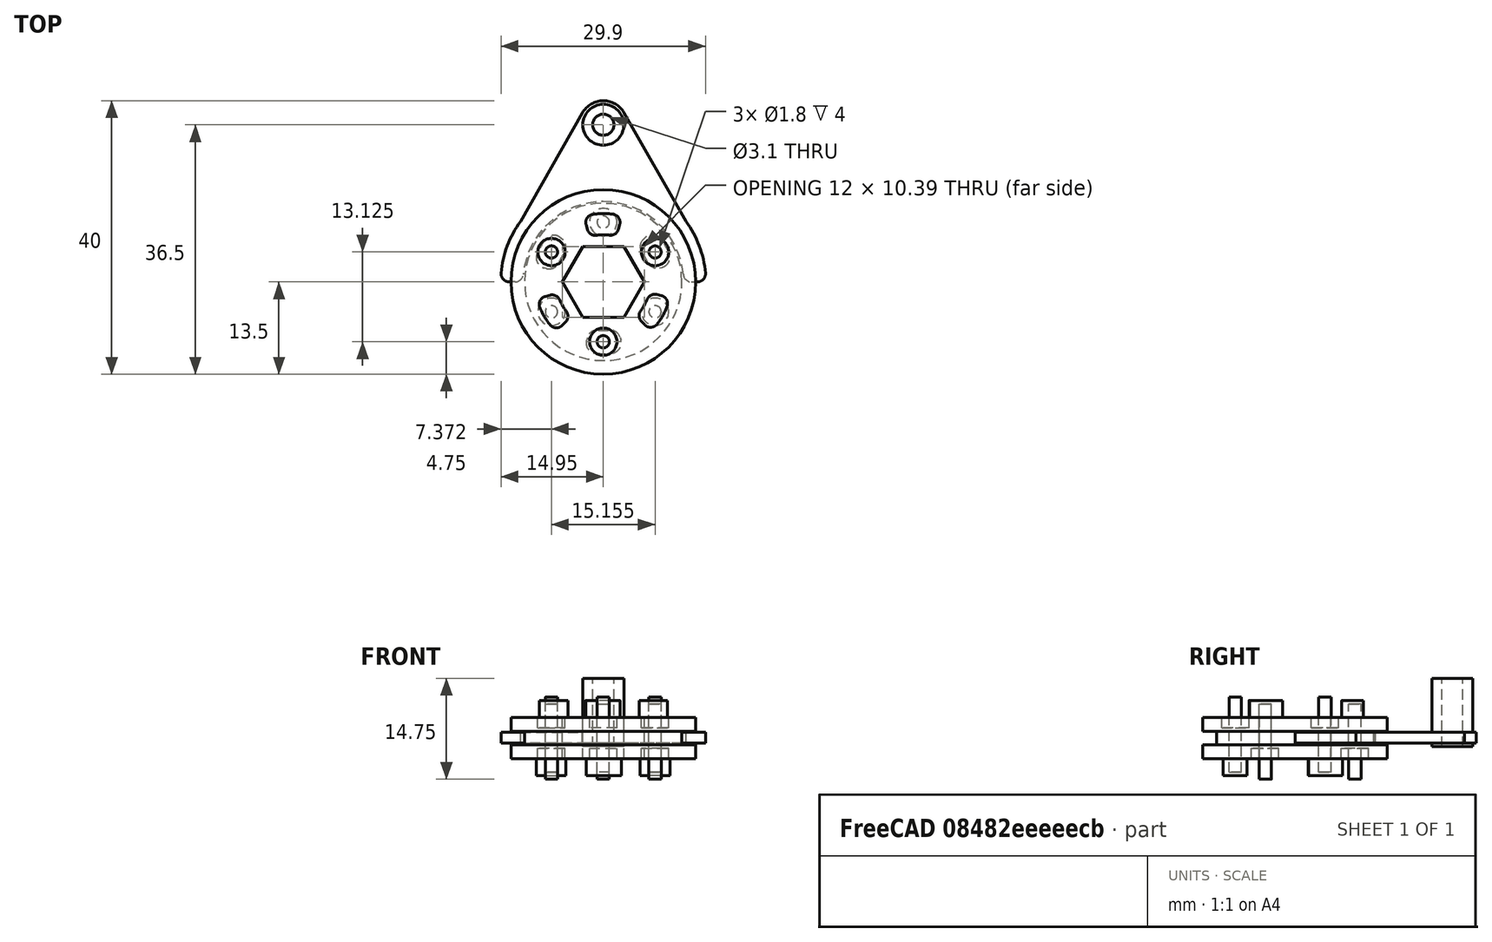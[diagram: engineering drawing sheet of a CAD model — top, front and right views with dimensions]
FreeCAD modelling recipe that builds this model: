
FCSTD DOCUMENT  (FreeCAD 0.16R5694 (Git))
Label: gearbox-selector
License: All rights reserved
LicenseURL: http://en.wikipedia.org/wiki/All_rights_reserved
objects: Part::Cylinder×44, Part::MultiFuse×15, Part::Cut×12, Part::Fillet×7, Part::Box×5, Part::Feature×3, Part::Extrusion×3, Part::RegularPolygon×1, Part::Mirroring×1
note: 91 computed .brp shape members not serialized (recipe doc carries the construction recipe); baked Part::Feature solids carry a one-line shape summary decoded from their .brp

FEATURE [Part::Cylinder] Cylinder
  Angle = 360
  Height = 2
  Radius = 13.5
FEATURE [Part::RegularPolygon] RegularPolygon  label="Regular polygon"
  Circumradius = 6
  Polygon = 6
FEATURE [Part::Feature] Face
  shape: bbox 18.03 x 18.03 x 2e-07 mm, 1 faces, 0 solids (baked)
FEATURE [Part::Extrusion] Extrude
  Base = -> Face
  Dir = (0,0,6)
  Solid = false
FEATURE [Part::Cylinder] Cylinder001
  Angle = 360
  Height = 2
  Placement = pos=(0,0,2) rot=(0,0,1;0rad)
  Radius = 11.5
FEATURE [Part::Cylinder] Cylinder002
  Angle = 360
  Height = 2
  Placement = pos=(0,0,4) rot=(0,0,1;0rad)
  Radius = 13.5
FEATURE [Part::Feature] Face001
  shape: bbox 18.03 x 18.03 x 2e-07 mm, 1 faces, 0 solids (baked)
FEATURE [Part::Extrusion] Extrude001
  Base = -> Face001
  Dir = (0,0,6)
  Solid = false
FEATURE [Part::Cut] Cut
  Base = -> Cylinder001
  Tool = -> Extrude
FEATURE [Part::Feature] Face002
  shape: bbox 18.03 x 18.03 x 2e-07 mm, 1 faces, 0 solids (baked)
FEATURE [Part::Extrusion] Extrude002
  Base = -> Face002
  Dir = (0,0,6)
  Solid = false
FEATURE [Part::Cut] Cut001
  Base = -> Cylinder
  Tool = -> Extrude001
FEATURE [Part::Cut] Cut002
  Base = -> Cylinder002
  Tool = -> Extrude002
FEATURE [Part::Cylinder] Cylinder003
  Angle = 32.74
  Height = 2.5
  Radius = 10.5
FEATURE [Part::Cylinder] Cylinder004
  Angle = 32.74
  Height = 2.5
  Radius = 7.1
FEATURE [Part::Cut] Cut003
  Base = -> Cylinder003
  Placement = pos=(0,0,-2.5) rot=(0,0,1;0.244346rad)
  Tool = -> Cylinder004
FEATURE [Part::Fillet] Fillet
  Base = -> Cut003
  Edges = 4 edges r=1.5: [Edge2,Edge4,Edge9,Edge12]
FEATURE [Part::Cylinder] Cylinder005
  Angle = 32.74
  Height = 2.5
  Radius = 10
FEATURE [Part::Cylinder] Cylinder006
  Angle = 32.74
  Height = 2.5
  Radius = 6.9
FEATURE [Part::Cut] Cut004
  Base = -> Cylinder005
  Placement = pos=(0,0,-2.5) rot=(0,0,1;0.244346rad)
  Tool = -> Cylinder006
FEATURE [Part::Fillet] Fillet001
  Base = -> Cut004
  Edges = 4 edges r=1.2: [Edge2,Edge4,Edge9,Edge12]
  Placement = pos=(0,0,8.5) rot=(0,0,1;0rad)
FEATURE [Part::Cylinder] Cylinder007
  Angle = 32.74
  Height = 2.5
  Radius = 10.5
FEATURE [Part::Cylinder] Cylinder008
  Angle = 32.74
  Height = 2.5
  Radius = 7.1
FEATURE [Part::Cut] Cut005
  Base = -> Cylinder007
  Placement = pos=(0,0,-2.5) rot=(0,0,1;0.244346rad)
  Tool = -> Cylinder008
FEATURE [Part::Fillet] Fillet002
  Base = -> Cut005
  Edges = 4 edges r=1.5: [Edge2,Edge4,Edge9,Edge12]
  Placement = pos=(0,0,0) rot=(0,0,1;2.0944rad)
FEATURE [Part::Cylinder] Cylinder009
  Angle = 32.74
  Height = 2.5
  Radius = 10.5
FEATURE [Part::Cylinder] Cylinder010
  Angle = 32.74
  Height = 2.5
  Radius = 7.1
FEATURE [Part::Cut] Cut006
  Base = -> Cylinder009
  Placement = pos=(0,0,-2.5) rot=(0,0,1;0.244346rad)
  Tool = -> Cylinder010
FEATURE [Part::Fillet] Fillet003
  Base = -> Cut006
  Edges = 4 edges r=1.5: [Edge2,Edge4,Edge9,Edge12]
  Placement = pos=(0,0,0) rot=(0,0,-1;2.0944rad)
FEATURE [Part::MultiFuse] Fusion
  Shapes = -> [Fillet003,Fillet002,Fillet]
FEATURE [Part::Cylinder] Cylinder011
  Angle = 32.74
  Height = 2.5
  Radius = 10
FEATURE [Part::Cylinder] Cylinder012
  Angle = 32.74
  Height = 2.5
  Radius = 6.9
FEATURE [Part::Cut] Cut007
  Base = -> Cylinder011
  Placement = pos=(0,0,-2.5) rot=(0,0,1;0.244346rad)
  Tool = -> Cylinder012
FEATURE [Part::Fillet] Fillet004
  Base = -> Cut007
  Edges = 4 edges r=1.2: [Edge2,Edge4,Edge9,Edge12]
  Placement = pos=(0,0,8.5) rot=(0,0,1;2.0944rad)
FEATURE [Part::Cylinder] Cylinder013
  Angle = 32.74
  Height = 2.5
  Radius = 10
FEATURE [Part::Cylinder] Cylinder014
  Angle = 32.74
  Height = 2.5
  Radius = 6.9
FEATURE [Part::Cut] Cut008
  Base = -> Cylinder013
  Placement = pos=(0,0,-2.5) rot=(0,0,1;0.244346rad)
  Tool = -> Cylinder014
FEATURE [Part::Fillet] Fillet005
  Base = -> Cut008
  Edges = 4 edges r=1.2: [Edge2,Edge4,Edge9,Edge12]
  Placement = pos=(0,0,8.5) rot=(0,0,-1;2.0944rad)
FEATURE [Part::MultiFuse] Fusion001
  Placement = pos=(0,0,0) rot=(0,0,1;1.0472rad)
  Shapes = -> [Fillet001,Fillet004,Fillet005]
FEATURE [Part::Cylinder] Cylinder015
  Angle = 360
  Height = 11
  Placement = pos=(0,-8.75,-2.5) rot=(0,0,1;0rad)
  Radius = 0.9
FEATURE [Part::Cylinder] Cylinder016
  Angle = 360
  Height = 11
  Placement = pos=(7.57772,-4.375,-2.5) rot=(0,0,1;1.0472rad)
  Radius = 0.9
FEATURE [Part::Cylinder] Cylinder017
  Angle = 360
  Height = 11
  Placement = pos=(7.57772,4.375,-2.5) rot=(0,0,1;2.0944rad)
  Radius = 0.9
FEATURE [Part::Cylinder] Cylinder018
  Angle = 360
  Height = 11
  Placement = pos=(0,8.75,-2.5) rot=(0,0,1;3.14159rad)
  Radius = 0.9
FEATURE [Part::Cylinder] Cylinder019
  Angle = 360
  Height = 11
  Placement = pos=(-7.57772,4.375,-2.5) rot=(0,0,1;4.18879rad)
  Radius = 0.9
FEATURE [Part::Cylinder] Cylinder020
  Angle = 360
  Height = 11
  Placement = pos=(-7.57772,-4.375,-2.5) rot=(0,0,-1;1.0472rad)
  Radius = 0.9
FEATURE [Part::MultiFuse] Fusion002
  Placement = pos=(0,0,0.5) rot=(0,0,1;0rad)
  Shapes = -> [Cylinder015,Cylinder017,Cylinder019]
FEATURE [Part::MultiFuse] Fusion003
  Placement = pos=(0,0,-0.5) rot=(0,0,1;0rad)
  Shapes = -> [Cylinder016,Cylinder018,Cylinder020]
FEATURE [Part::MultiFuse] Fusion004
  Shapes = -> [Cut001,Fusion]
FEATURE [Part::MultiFuse] Fusion005
  Shapes = -> [Cut002,Fusion001]
FEATURE [Part::Cylinder] Cylinder021
  Angle = 360
  Height = 1.5
  Placement = pos=(0,-8.75,-2.5) rot=(0,0,1;0rad)
  Radius = 2
FEATURE [Part::Cylinder] Cylinder022
  Angle = 360
  Height = 1.5
  Placement = pos=(7.57772,4.375,-2.5) rot=(0,0,1;2.0944rad)
  Radius = 2
FEATURE [Part::Cylinder] Cylinder023
  Angle = 360
  Height = 1.5
  Placement = pos=(-7.57772,4.375,-2.5) rot=(0,0,-1;2.0944rad)
  Radius = 2
FEATURE [Part::MultiFuse] Fusion006
  Placement = pos=(0,0,7) rot=(0,0,1;0rad)
  Shapes = -> [Cylinder021,Cylinder022,Cylinder023]
FEATURE [Part::Cylinder] Cylinder024
  Angle = 360
  Height = 11
  Placement = pos=(0,-8.75,-2.5) rot=(0,0,1;0rad)
  Radius = 0.9
FEATURE [Part::Cylinder] Cylinder025
  Angle = 360
  Height = 11
  Placement = pos=(7.57772,4.375,-2.5) rot=(0,0,1;2.0944rad)
  Radius = 0.9
FEATURE [Part::Cylinder] Cylinder026
  Angle = 360
  Height = 11
  Placement = pos=(-7.57772,4.375,-2.5) rot=(0,0,1;4.18879rad)
  Radius = 0.9
FEATURE [Part::MultiFuse] Fusion007
  Placement = pos=(0,0,0.5) rot=(0,0,1;0rad)
  Shapes = -> [Cylinder024,Cylinder025,Cylinder026]
FEATURE [Part::Cylinder] Cylinder027
  Angle = 360
  Height = 11
  Placement = pos=(0,-8.75,-2.5) rot=(0,0,1;0rad)
  Radius = 0.9
FEATURE [Part::Cylinder] Cylinder028
  Angle = 360
  Height = 11
  Placement = pos=(7.57772,4.375,-2.5) rot=(0,0,1;2.0944rad)
  Radius = 0.9
FEATURE [Part::Cylinder] Cylinder029
  Angle = 360
  Height = 11
  Placement = pos=(-7.57772,4.375,-2.5) rot=(0,0,1;4.18879rad)
  Radius = 0.9
FEATURE [Part::MultiFuse] Fusion008
  Placement = pos=(0,0,0.5) rot=(0,0,1;0rad)
  Shapes = -> [Cylinder027,Cylinder028,Cylinder029]
FEATURE [Part::Cut] Cut012
  Base = -> Fusion004
  Tool = -> Fusion002
FEATURE [Part::Cylinder] Cylinder030
  Angle = 360
  Height = 1.5
  Placement = pos=(7.57772,-4.375,-2.5) rot=(0,0,1;1.0472rad)
  Radius = 2
FEATURE [Part::Cylinder] Cylinder031
  Angle = 360
  Height = 1.5
  Placement = pos=(0,8.75,-2.5) rot=(0,0,1;3.14159rad)
  Radius = 2
FEATURE [Part::Cylinder] Cylinder032
  Angle = 360
  Height = 1.5
  Placement = pos=(-7.57772,-4.375,-2.5) rot=(0,0,-1;1.0472rad)
  Radius = 2
FEATURE [Part::MultiFuse] Fusion009
  Placement = pos=(0,0,2.5) rot=(0,0,1;0rad)
  Shapes = -> [Cylinder030,Cylinder031,Cylinder032]
FEATURE [Part::Cylinder] Cylinder033
  Angle = 360
  Height = 11
  Placement = pos=(7.57772,-4.375,-2.5) rot=(0,0,1;1.0472rad)
  Radius = 0.9
FEATURE [Part::Cylinder] Cylinder034
  Angle = 360
  Height = 11
  Placement = pos=(0,8.75,-2.5) rot=(0,0,1;3.14159rad)
  Radius = 0.9
FEATURE [Part::Cylinder] Cylinder035
  Angle = 360
  Height = 11
  Placement = pos=(-7.57772,-4.375,-2.5) rot=(0,0,-1;1.0472rad)
  Radius = 0.9
FEATURE [Part::MultiFuse] Fusion010
  Placement = pos=(0,0,-0.5) rot=(0,0,1;0rad)
  Shapes = -> [Cylinder033,Cylinder034,Cylinder035]
FEATURE [Part::Cylinder] Cylinder036
  Angle = 360
  Height = 11
  Placement = pos=(7.57772,-4.375,-2.5) rot=(0,0,1;1.0472rad)
  Radius = 0.9
FEATURE [Part::Cylinder] Cylinder037
  Angle = 360
  Height = 11
  Placement = pos=(0,8.75,-2.5) rot=(0,0,1;3.14159rad)
  Radius = 0.9
FEATURE [Part::Cylinder] Cylinder038
  Angle = 360
  Height = 11
  Placement = pos=(-7.57772,-4.375,-2.5) rot=(0,0,-1;1.0472rad)
  Radius = 0.9
FEATURE [Part::MultiFuse] Fusion011
  Placement = pos=(0,0,-0.5) rot=(0,0,1;0rad)
  Shapes = -> [Cylinder036,Cylinder037,Cylinder038]
FEATURE [Part::Cylinder] Cylinder039
  Angle = 180
  Height = 1.6
  Radius = 15
FEATURE [Part::Cylinder] Cylinder040
  Angle = 180
  Height = 1.6
  Radius = 11.75
FEATURE [Part::Cut] Cut017
  Base = -> Cylinder039
  Tool = -> Cylinder040
FEATURE [Part::Cylinder] Cylinder042
  Angle = 360
  Height = 10
  Placement = pos=(0,23,-0.5) rot=(0,0,1;0rad)
  Radius = 3
FEATURE [Part::Cylinder] Cylinder043
  Angle = 360
  Height = 1.6
  Placement = pos=(0,23,0) rot=(0,0,1;0rad)
  Radius = 3.5
FEATURE [Part::Cylinder] Cylinder044
  Angle = 360
  Height = 10
  Placement = pos=(0,23,-0.5) rot=(0,0,1;0rad)
  Radius = 1.55
FEATURE [Part::Box] Box  label="Cube"
  Height = 1.6
  Length = 7
  Placement = pos=(-3.5,12,0) rot=(0,0,1;0rad)
  Width = 11
FEATURE [Part::Box] Box001  label="Cube001"
  Height = 1.6
  Length = 2
  Placement = pos=(12,5,0) rot=(0,0,1;0.518363rad)
  Width = 21.6
FEATURE [Part::Box] Box002  label="Cube002"
  Height = 1.6
  Length = 2
  Placement = pos=(12,5,0) rot=(0,0,1;0.518363rad)
  Width = 21.6
FEATURE [Part::Mirroring] Part__Mirroring  label="Cube002 (Mirror #1)"
  Base = (0,0,0)
  Normal = (1,0,0)
  Source = -> Box002
FEATURE [Part::Box] Box003  label="Cube003"
  Height = 1.6
  Length = 11
  Placement = pos=(-5.5,16,0) rot=(0,0,1;0rad)
  Width = 4
FEATURE [Part::Box] Box004  label="Cube004"
  Height = 1.6
  Length = 15
  Placement = pos=(-7.5,12,0) rot=(0,0,1;0rad)
  Width = 4.55
FEATURE [Part::MultiFuse] Fusion012
  Shapes = -> [Cut017,Cylinder043,Box,Box001,Part__Mirroring,Box004,Box003]
FEATURE [Part::MultiFuse] Fusion013
  Shapes = -> [Fusion012,Cylinder042]
FEATURE [Part::Cut] Cut018
  Base = -> Fusion013
  Tool = -> Cylinder044
FEATURE [Part::Fillet] Fillet006
  Base = -> Cut018
  Edges = 4 edges r=1.2: [Edge18,Edge20,Edge21,Edge25]
  Placement = pos=(0,0,2.25) rot=(0,0,1;0rad)
FEATURE [Part::MultiFuse] Fusion014
  Shapes = -> [Fusion005,Cut,Cut012]
